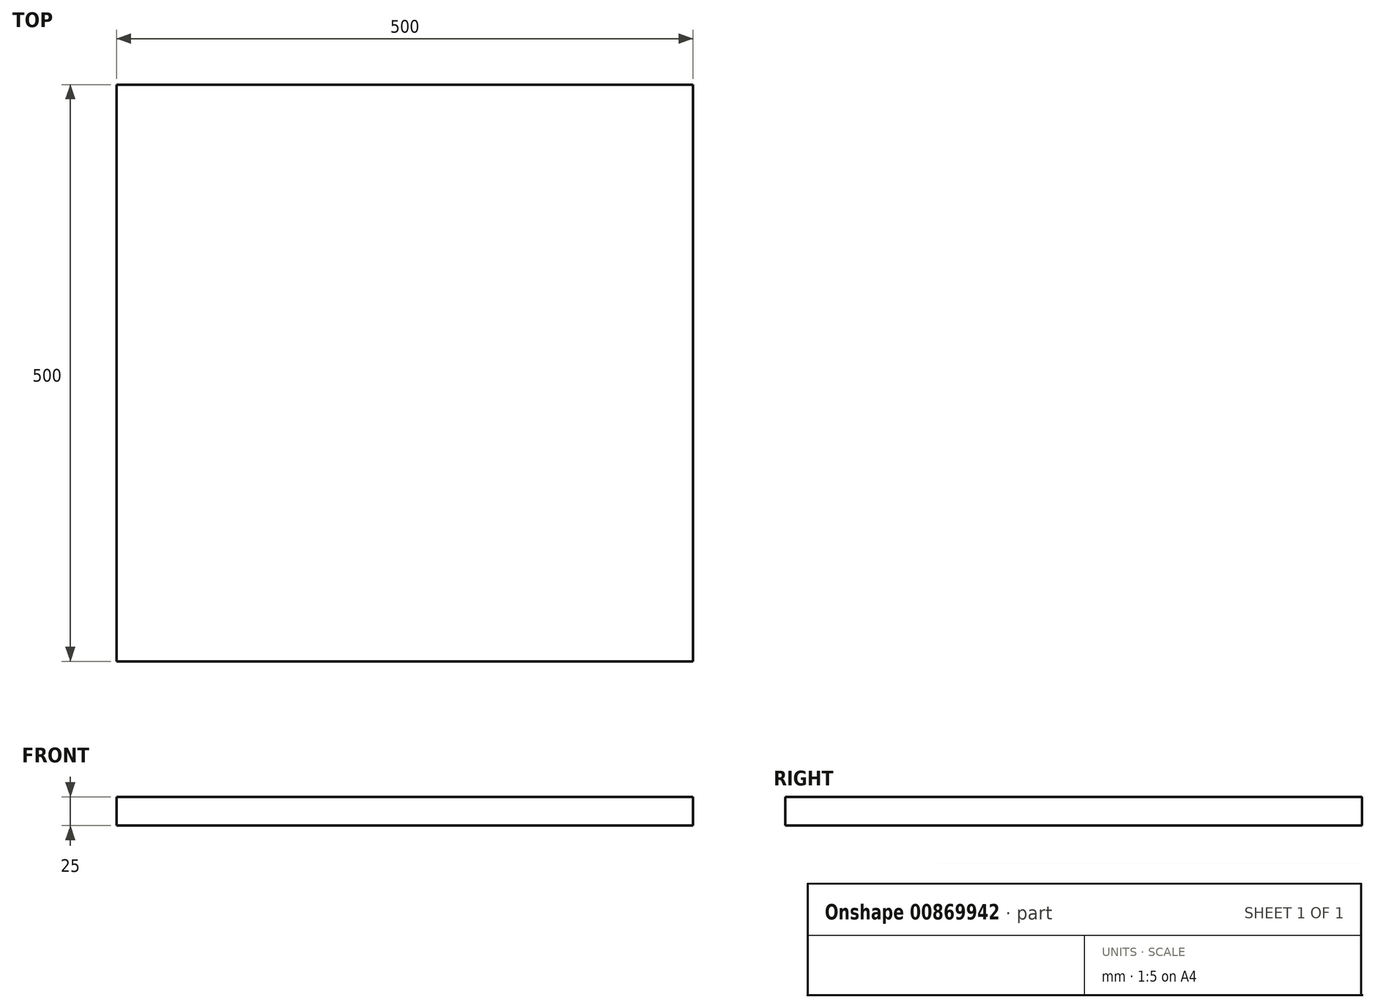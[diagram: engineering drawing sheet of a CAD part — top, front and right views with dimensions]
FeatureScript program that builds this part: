
annotation { "Feature Type Name" : "Feature", "Feature Type Description" : "" }
export const myFeature = defineFeature(function(context is Context, id is Id, definition is map)
    precondition{}
    {
        {
            var Q0;
            Q0=qCreatedBy(makeId("Top.planeOp"),FACE);
            var sketch = newSketch(context, id + "F0", { "sketchPlane" : qUnion([Q0])});
            skLineSegment(sketch, "E0.bottom", {"start": v(-250, 250) * mm, "end": v(250, 250) * mm});
            skLineSegment(sketch, "E0.top", {"start": v(-250, -250) * mm, "end": v(250, -250) * mm});
            skLineSegment(sketch, "E0.left", {"start": v(-250, 250) * mm, "end": v(-250, -250) * mm});
            skLineSegment(sketch, "E0.right", {"start": v(250, 250) * mm, "end": v(250, -250) * mm});
            skLineSegment(sketch, "E1", {"start": v(0, 250) * mm, "end": v(0, -250) * mm, "construction": true});
            skSolve(sketch);
        }
        {
            var Q0;
            Q0=makeQuery(id+"F0.imprint","IMPRINT",FACE,{"disambiguationData":[TD([[makeQuery(id+"F0.imprint","IMPRINT",EDGE,{"derivedFrom":sQuery(id+"F0.wireOp",EDGE,"E0.bottom")}),-1.0]])]});
            extrude(context, id + "F1", {"entities" : qUnion([Q0]), "depth" : 25 * mm, "offsetDistance" : 25 * mm});
        }
    });
